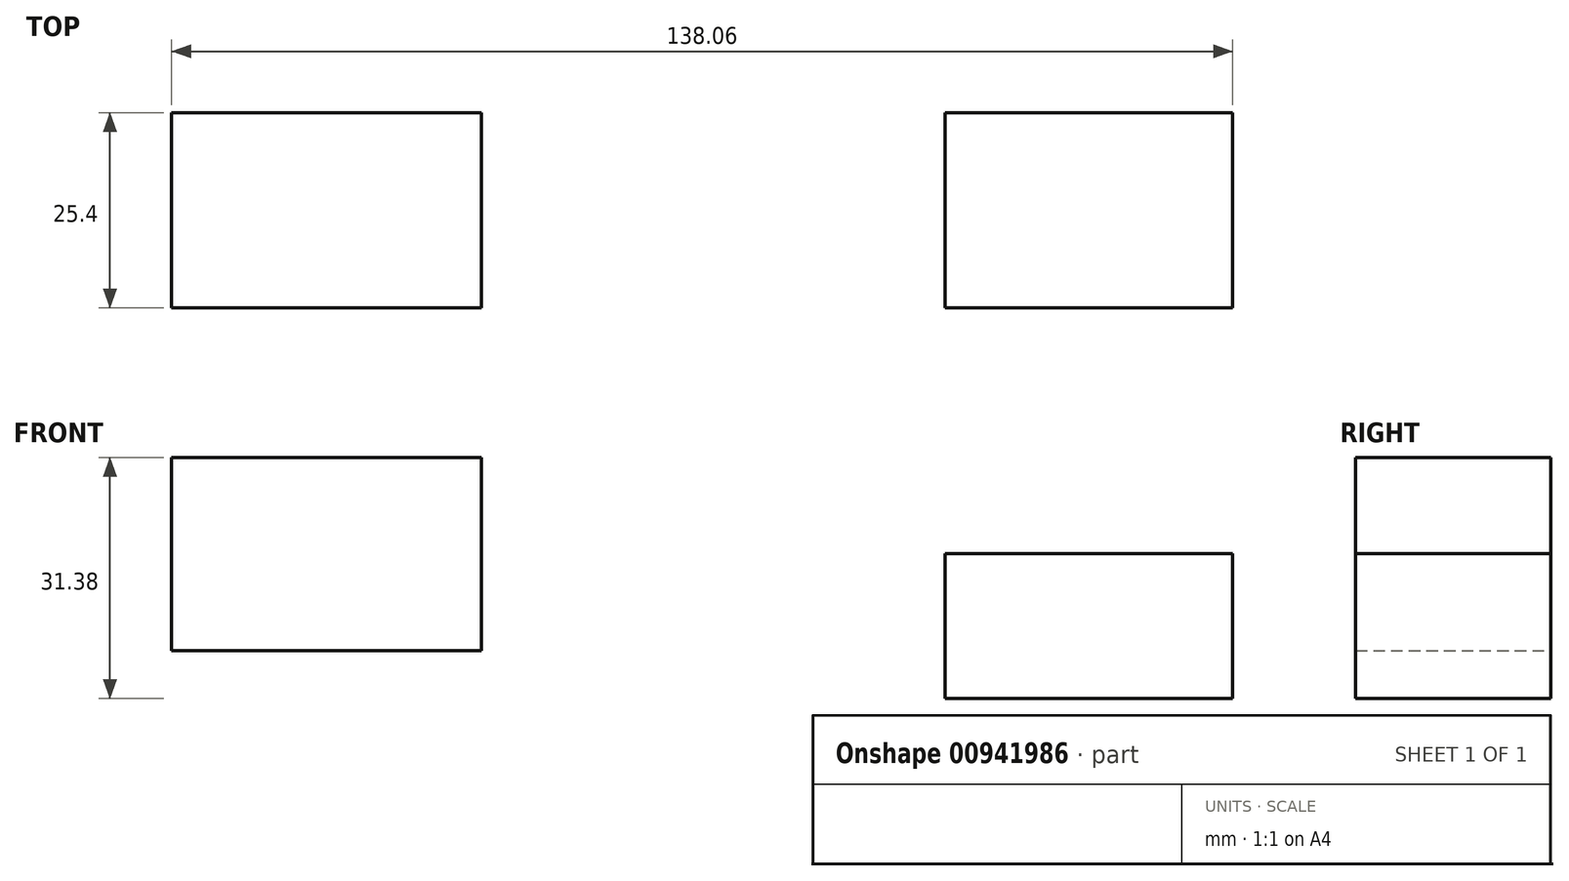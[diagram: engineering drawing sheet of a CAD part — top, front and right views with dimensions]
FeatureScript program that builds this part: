
annotation { "Feature Type Name" : "Feature", "Feature Type Description" : "" }
export const myFeature = defineFeature(function(context is Context, id is Id, definition is map)
    precondition{}
    {
        {
            var Q0;
            Q0=qCreatedBy(makeId("Front.planeOp"),FACE);
            var sketch = newSketch(context, id + "F0", { "sketchPlane" : qUnion([Q0])});
            skLineSegment(sketch, "E0.bottom", {"start": v(-85.77, 47.64) * mm, "end": v(-45.46, 47.64) * mm});
            skLineSegment(sketch, "E0.top", {"start": v(-85.77, 22.5) * mm, "end": v(-45.46, 22.5) * mm});
            skLineSegment(sketch, "E0.left", {"start": v(-85.77, 47.64) * mm, "end": v(-85.77, 22.5) * mm});
            skLineSegment(sketch, "E0.right", {"start": v(-45.46, 47.64) * mm, "end": v(-45.46, 22.5) * mm});
            skLineSegment(sketch, "E1.bottom", {"start": v(14.9, 35.13) * mm, "end": v(52.29, 35.13) * mm});
            skLineSegment(sketch, "E1.top", {"start": v(14.9, 16.26) * mm, "end": v(52.29, 16.26) * mm});
            skLineSegment(sketch, "E1.left", {"start": v(14.9, 35.13) * mm, "end": v(14.9, 16.26) * mm});
            skLineSegment(sketch, "E1.right", {"start": v(52.29, 35.13) * mm, "end": v(52.29, 16.26) * mm});
            skSolve(sketch);
        }
        {
            var Q0;
            Q0 = qSketchRegion(id + "F0", true);
            extrude(context, id + "F1", {"entities" : qUnion([Q0]), "depth" : 25.4 * mm, "offsetDistance" : 25.4 * mm});
        }
    });
